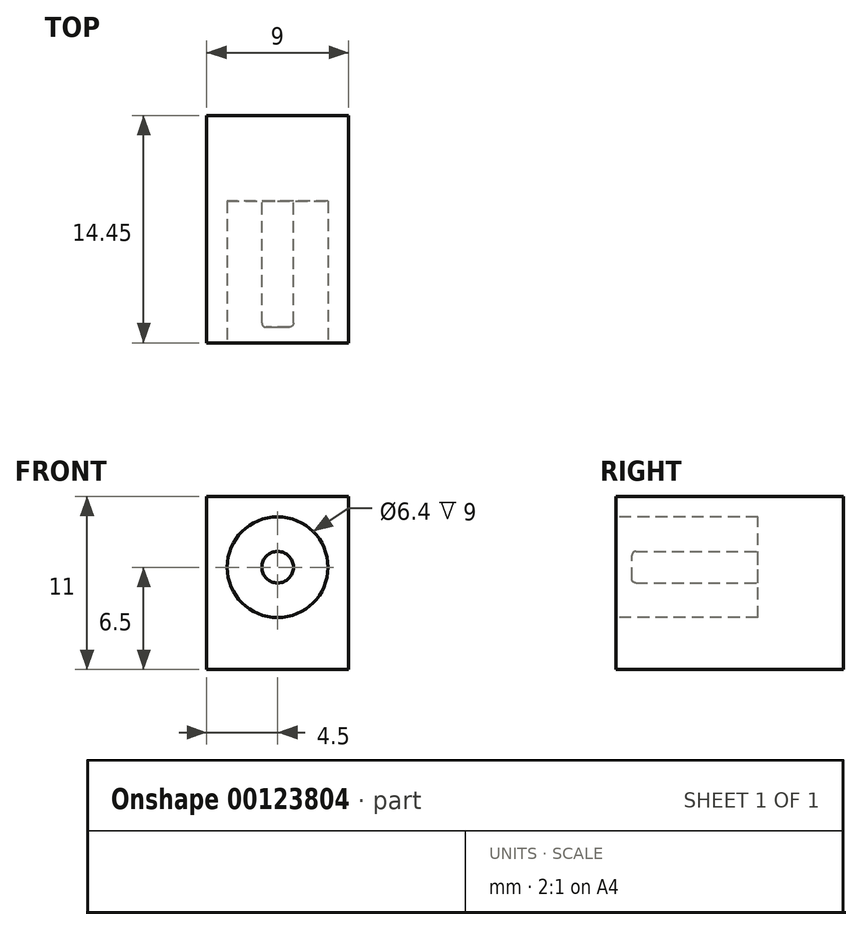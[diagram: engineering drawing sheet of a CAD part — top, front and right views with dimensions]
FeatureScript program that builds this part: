
annotation { "Feature Type Name" : "Feature", "Feature Type Description" : "" }
export const myFeature = defineFeature(function(context is Context, id is Id, definition is map)
    precondition{}
    {
        {
            var Q0;
            Q0=qCreatedBy(makeId("Front.planeOp"),FACE);
            var sketch = newSketch(context, id + "F0", { "sketchPlane" : qUnion([Q0])});
            skCircle(sketch, "E0", {"center": v(0, 0) * mm, "radius": 3.2 * mm, "construction": true});
            skLineSegment(sketch, "E1.bottom", {"start": v(-4.5, 4.5) * mm, "end": v(4.5, 4.5) * mm});
            skLineSegment(sketch, "E1.top", {"start": v(-4.5, -6.5) * mm, "end": v(4.5, -6.5) * mm});
            skLineSegment(sketch, "E1.left", {"start": v(-4.5, 4.5) * mm, "end": v(-4.5, -6.5) * mm});
            skLineSegment(sketch, "E1.right", {"start": v(4.5, 4.5) * mm, "end": v(4.5, -6.5) * mm});
            skLineSegment(sketch, "E2", {"start": v(0, 4.5) * mm, "end": v(0, -6.5) * mm, "construction": true});
            skLineSegment(sketch, "E3", {"start": v(-4.5, 0) * mm, "end": v(4.5, 0) * mm, "construction": true});
            skSolve(sketch);
        }
        {
            var Q0;
            Q0=makeQuery(id+"F0.imprint","IMPRINT",FACE,{"disambiguationData":[TD([[makeQuery(id+"F0.imprint","IMPRINT",EDGE,{"derivedFrom":sQuery(id+"F0.wireOp",EDGE,"E0")}),-1.0]])]});
            var Q1;
            Q1=makeQuery(id+"F0.imprint","IMPRINT",FACE,{"disambiguationData":[TD([[makeQuery(id+"F0.imprint","IMPRINT",EDGE,{"derivedFrom":sQuery(id+"F0.wireOp",EDGE,"E1.bottom")}),-1.0]])]});
            extrude(context, id + "F1", {"entities" : qUnion([Q0, Q1]), "oppositeDirection" : true, "depth" : 3.45 * mm});
        }
        {
            var Q0;
            Q0=makeQuery(id+"F1.opExtrude","CAP_FACE",FACE,{"disambiguationData":[OSD([sQuery(id+"F0.wireOp",EDGE,"E1.bottom"),sQuery(id+"F0.wireOp",EDGE,"E1.top"),sQuery(id+"F0.wireOp",EDGE,"E1.left"),sQuery(id+"F0.wireOp",EDGE,"E1.right")])],"isStart":false});
            var sketch = newSketch(context, id + "F2", { "sketchPlane" : qUnion([Q0])});
            skArc(sketch, "E4", {"start": v(-4, 0) * mm, "mid": v(0, 4) * mm, "end": v(4, 0) * mm});
            skLineSegment(sketch, "E5", {"start": v(-4, 0) * mm, "end": v(-4.5, 0) * mm});
            skLineSegment(sketch, "E6", {"start": v(-4.5, 0) * mm, "end": v(-4.5, -6.5) * mm});
            skLineSegment(sketch, "E7", {"start": v(-4.5, -6.5) * mm, "end": v(4.5, -6.5) * mm});
            skLineSegment(sketch, "E8", {"start": v(4.5, -6.5) * mm, "end": v(4.5, 0) * mm});
            skLineSegment(sketch, "E9", {"start": v(4.5, 0) * mm, "end": v(4, 0) * mm});
            skSolve(sketch);
        }
        {
            var Q0;
            Q0 = qSketchRegion(id + "F2", true);
            var Q1;
            Q1=makeQuery(id+"F2.imprint","IMPRINT",FACE,{"disambiguationData":[TD([[makeQuery(id+"F2.imprint","IMPRINT",EDGE,{"derivedFrom":sQuery(id+"F2.wireOp",EDGE,"E4")}),-1.0]])]});
            extrude(context, id + "F3", {"entities" : qUnion([Q0, Q1]), "operationType" : NewBodyOperationType.ADD, "depth" : 11 * mm});
        }
        {
            var Q0;
            Q0=makeQuery(id+"F1.opExtrude","CAP_FACE",FACE,{"disambiguationData":[OSD([sQuery(id+"F0.wireOp",EDGE,"E1.bottom"),sQuery(id+"F0.wireOp",EDGE,"E1.top"),sQuery(id+"F0.wireOp",EDGE,"E1.left"),sQuery(id+"F0.wireOp",EDGE,"E1.right")])],"isStart":true});
            var sketch = newSketch(context, id + "F4", { "sketchPlane" : qUnion([Q0])});
            skCircle(sketch, "E10.0", {"center": v(0, 0) * mm, "radius": 3.2 * mm});
            skSolve(sketch);
        }
        {
            var Q0;
            Q0=makeQuery(id+"F4.imprint","IMPRINT",FACE,{"disambiguationData":[TD([[makeQuery(id+"F4.imprint","IMPRINT",EDGE,{"derivedFrom":sQuery(id+"F4.wireOp",EDGE,"E10.0")}),1.0]])]});
            var Q1;
            Q1=sQuery(id+"F4.wireOp",EDGE,"E10.0");
            extrude(context, id + "F5", {"entities" : qUnion([Q0]), "operationType" : NewBodyOperationType.REMOVE, "surfaceEntities" : qUnion([Q1]), "oppositeDirection" : true, "depth" : 9 * mm});
        }
        {
            var Q0;
            Q0=makeQuery(id+"F5.boolean.opBoolean","COPY",FACE,{"derivedFrom":makeQuery(id+"F5.opExtrude","CAP_FACE",FACE,{"disambiguationData":[OSD([sQuery(id+"F4.wireOp",EDGE,"E10.0")])],"isStart":false})});
            var sketch = newSketch(context, id + "F6", { "sketchPlane" : qUnion([Q0])});
            skCircle(sketch, "E11", {"center": v(0, 0) * mm, "radius": 1 * mm});
            skSolve(sketch);
        }
        {
            var Q0;
            Q0=makeQuery(id+"F6.imprint","IMPRINT",FACE,{"disambiguationData":[TD([[makeQuery(id+"F6.imprint","IMPRINT",EDGE,{"derivedFrom":sQuery(id+"F6.wireOp",EDGE,"E11")}),1.0]])]});
            extrude(context, id + "F7", {"entities" : qUnion([Q0]), "operationType" : NewBodyOperationType.ADD, "depth" : 8 * mm});
        }
        {
            var Q0;
            Q0=makeQuery(id+"F7.opExtrude","CAP_EDGE",EDGE,{"disambiguationData":[OSD([sQuery(id+"F6.wireOp",EDGE,"E11")])],"isStart":false});
            fillet(context, id + "F8", {"entities" : qUnion([Q0]), "radius" : 0.25 * mm, "tangentPropagation" : true, "allowEdgeOverflow" : false});
        }
    });
